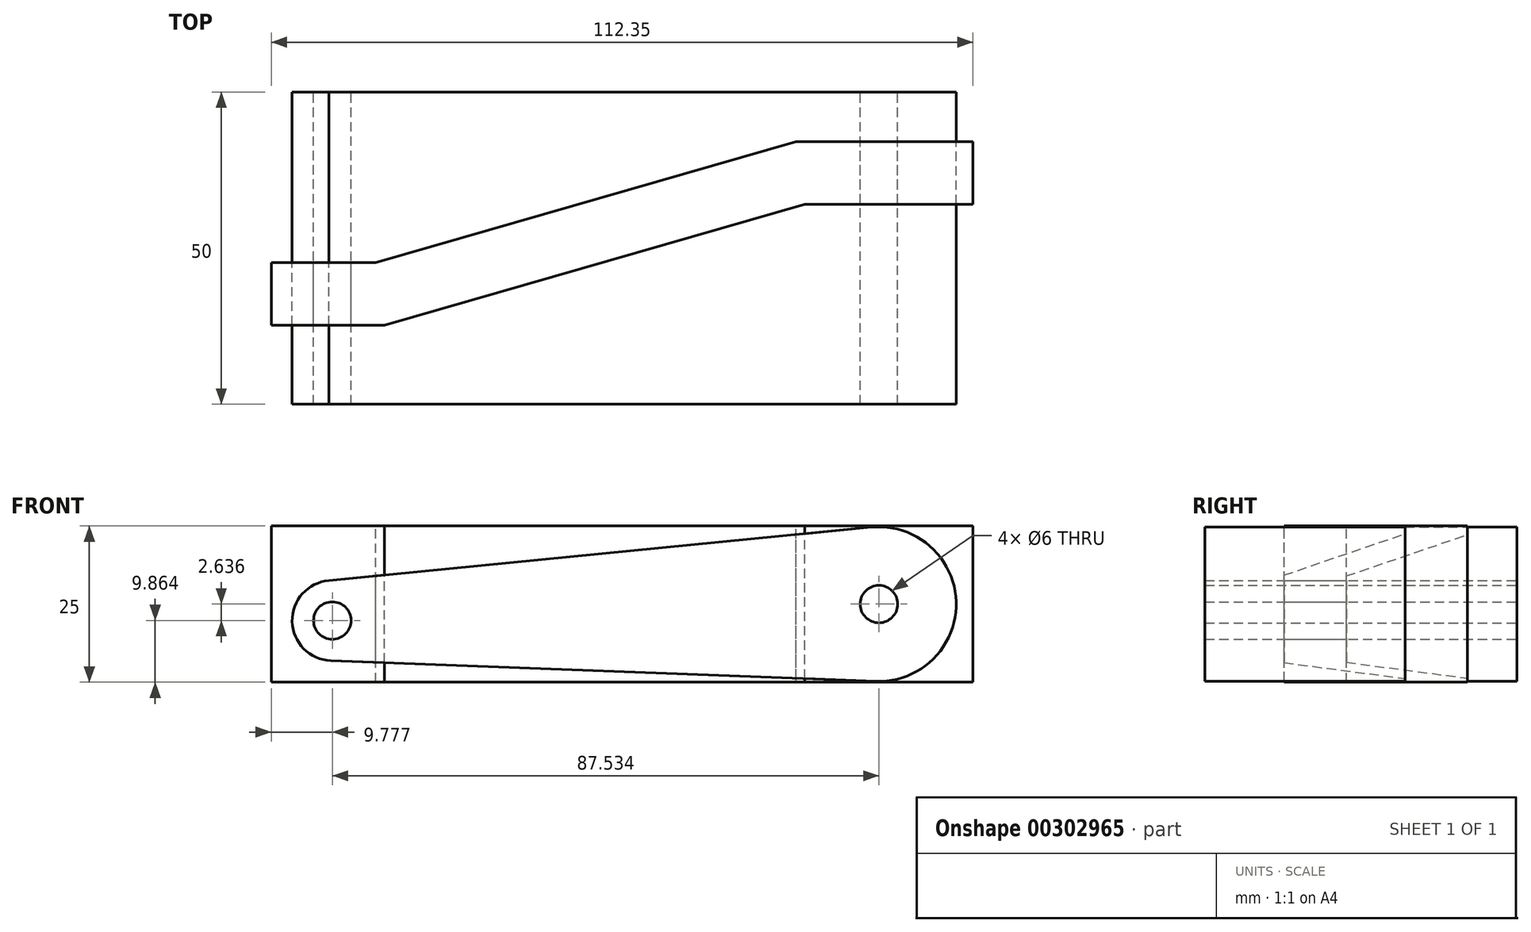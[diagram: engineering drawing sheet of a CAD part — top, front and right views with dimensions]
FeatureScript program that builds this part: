
annotation { "Feature Type Name" : "Feature", "Feature Type Description" : "" }
export const myFeature = defineFeature(function(context is Context, id is Id, definition is map)
    precondition{}
    {
        {
            var Q0;
            Q0=qCreatedBy(makeId("Front.planeOp"),FACE);
            var sketch = newSketch(context, id + "F0", { "sketchPlane" : qUnion([Q0])});
            skCircle(sketch, "E0", {"center": v(-49.15, -2.64) * mm, "radius": 6.42 * mm});
            skCircle(sketch, "E1", {"center": v(38.38, 0) * mm, "radius": 12.37 * mm});
            skCircle(sketch, "E2", {"center": v(-49.15, -2.64) * mm, "radius": 3 * mm});
            skCircle(sketch, "E3", {"center": v(38.38, 0) * mm, "radius": 3 * mm});
            skLineSegment(sketch, "E4", {"start": v(-49.7, 3.77) * mm, "end": v(37.17, 12.3) * mm});
            skLineSegment(sketch, "E5", {"start": v(-49.4, -9.06) * mm, "end": v(37.91, -12.36) * mm});
            skSolve(sketch);
        }
        {
            var Q0;
            Q0 = qSketchRegion(id + "F0", true);
            extrude(context, id + "F1", {"entities" : qUnion([Q0]), "depth" : 50 * mm, "offsetDistance" : 25 * mm});
        }
        {
            var Q0;
            Q0=qCreatedBy(makeId("Top.planeOp"),FACE);
            var sketch = newSketch(context, id + "F2", { "sketchPlane" : qUnion([Q0])});
            skLineSegment(sketch, "E6", {"start": v(-58.93, -37.33) * mm, "end": v(-40.82, -37.33) * mm});
            skLineSegment(sketch, "E7", {"start": v(-40.82, -37.33) * mm, "end": v(26.5, -17.95) * mm});
            skLineSegment(sketch, "E8", {"start": v(26.5, -17.95) * mm, "end": v(53.42, -17.95) * mm});
            skLineSegment(sketch, "E9.0", {"start": v(25.08, -7.95) * mm, "end": v(53.42, -7.95) * mm});
            skLineSegment(sketch, "E9.1", {"start": v(-42.23, -27.33) * mm, "end": v(25.08, -7.95) * mm});
            skLineSegment(sketch, "E9.2", {"start": v(-58.93, -27.33) * mm, "end": v(-42.23, -27.33) * mm});
            skLineSegment(sketch, "E10", {"start": v(-58.93, -37.33) * mm, "end": v(-58.93, -27.33) * mm});
            skLineSegment(sketch, "E11", {"start": v(53.42, -7.95) * mm, "end": v(53.42, -17.95) * mm});
            skSolve(sketch);
        }
        {
            var Q0;
            Q0 = qSketchRegion(id + "F2", true);
            extrude(context, id + "F3", {"entities" : qUnion([Q0]), "oppositeDirection" : true, "depth" : 25 * mm, "offsetDistance" : 25 * mm, "symmetric" : true});
        }
        {
            var Q0;
            Q0=makeQuery(id+"F1.opExtrude","SWEPT_BODY",BODY,{"disambiguationData":[OSD([sQuery(id+"F0.wireOp",EDGE,"E0"),sQuery(id+"F0.wireOp",EDGE,"E1"),sQuery(id+"F0.wireOp",EDGE,"E2"),sQuery(id+"F0.wireOp",EDGE,"E3"),sQuery(id+"F0.wireOp",EDGE,"E4"),sQuery(id+"F0.wireOp",EDGE,"E5")])]});
            var Q1;
            Q1=makeQuery(id+"F3.opExtrude","SWEPT_BODY",BODY,{"disambiguationData":[OSD([sQuery(id+"F2.wireOp",EDGE,"E6"),sQuery(id+"F2.wireOp",EDGE,"E7"),sQuery(id+"F2.wireOp",EDGE,"E8"),sQuery(id+"F2.wireOp",EDGE,"E9.0"),sQuery(id+"F2.wireOp",EDGE,"E9.1"),sQuery(id+"F2.wireOp",EDGE,"E9.2"),sQuery(id+"F2.wireOp",EDGE,"E10"),sQuery(id+"F2.wireOp",EDGE,"E11")])]});
            var Q2;
            Q2=makeQuery(id+"F3.opExtrude","SWEPT_BODY",BODY,{"disambiguationData":[OSD([sQuery(id+"F2.wireOp",EDGE,"E6"),sQuery(id+"F2.wireOp",EDGE,"E7"),sQuery(id+"F2.wireOp",EDGE,"E8"),sQuery(id+"F2.wireOp",EDGE,"E9.0"),sQuery(id+"F2.wireOp",EDGE,"E9.1"),sQuery(id+"F2.wireOp",EDGE,"E9.2"),sQuery(id+"F2.wireOp",EDGE,"E10"),sQuery(id+"F2.wireOp",EDGE,"E11")])]});
            booleanBodies(context, id + "F4", {"operationType" : BooleanOperationType.INTERSECTION, "tools" : qUnion([Q0, Q1]), "targets" : qUnion([Q2]), "keepTools" : true});
        }
    });
